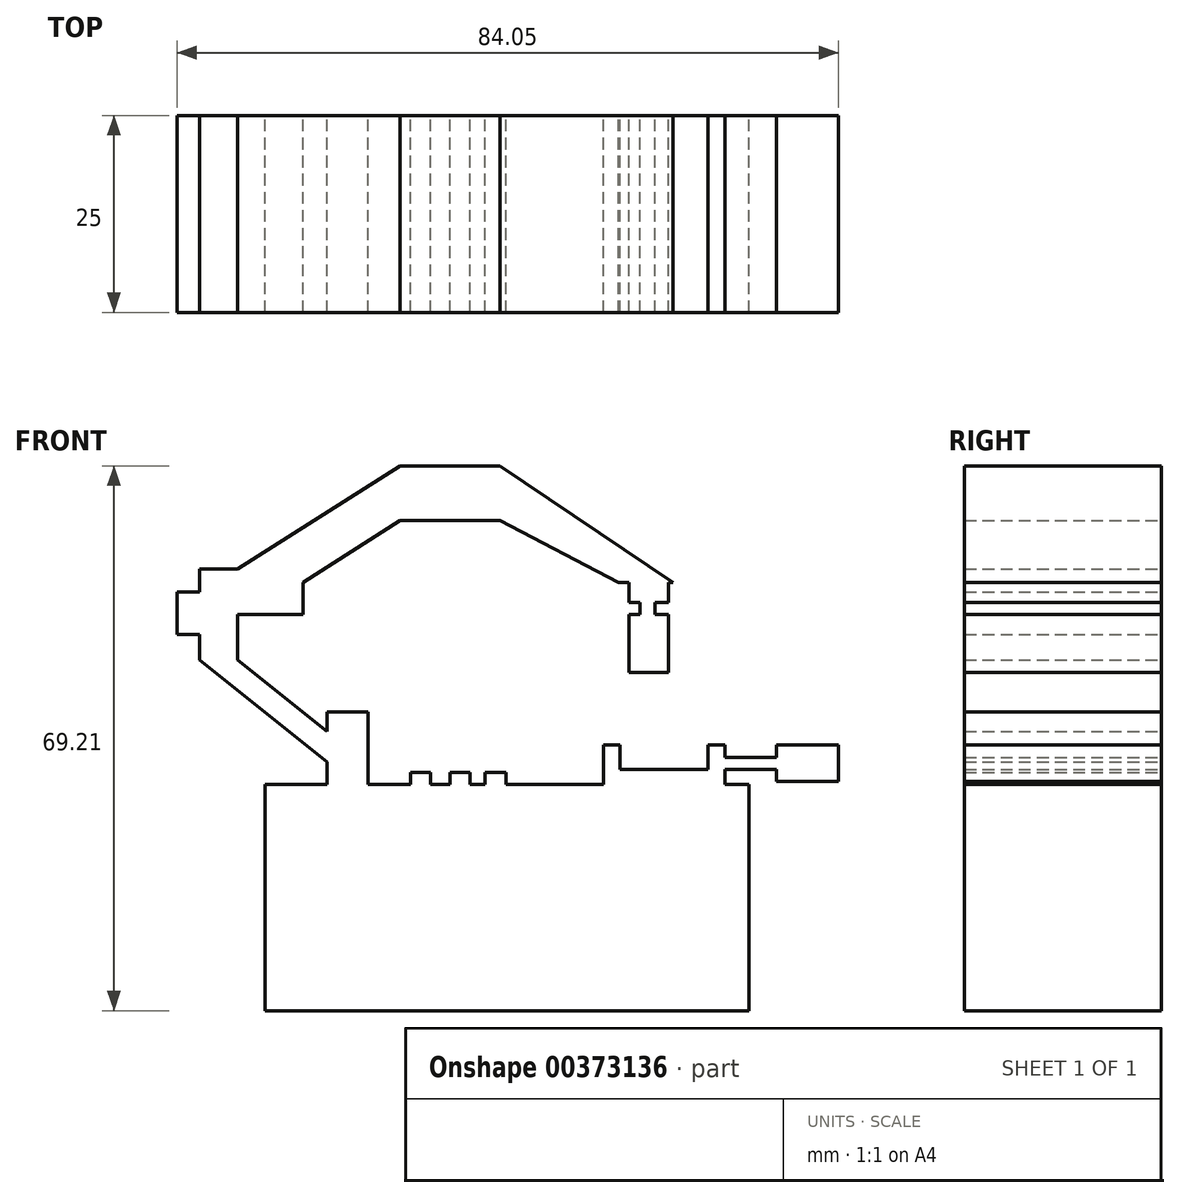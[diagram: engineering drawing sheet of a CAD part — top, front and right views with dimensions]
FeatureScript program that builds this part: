
annotation { "Feature Type Name" : "Feature", "Feature Type Description" : "" }
export const myFeature = defineFeature(function(context is Context, id is Id, definition is map)
    precondition{}
    {
        {
            var Q0;
            Q0=qCreatedBy(makeId("Front.planeOp"),FACE);
            var sketch = newSketch(context, id + "F0", { "sketchPlane" : qUnion([Q0])});
            skLineSegment(sketch, "E0", {"start": v(-61.5, 0) * mm, "end": v(-61.5, -14.36) * mm});
            skLineSegment(sketch, "E1", {"start": v(-61.5, -14.36) * mm, "end": v(0, -14.36) * mm});
            skLineSegment(sketch, "E2", {"start": v(-61.5, 0) * mm, "end": v(-61.5, 14.36) * mm});
            skLineSegment(sketch, "E3", {"start": v(-61.5, 14.36) * mm, "end": v(0, 14.36) * mm});
            skLineSegment(sketch, "E4", {"start": v(0, 14.36) * mm, "end": v(0, -14.36) * mm});
            skLineSegment(sketch, "E5", {"start": v(-61.5, 7.18) * mm, "end": v(-58.03, 9.16) * mm});
            skLineSegment(sketch, "E6", {"start": v(-58.03, 9.16) * mm, "end": v(-54.56, 9.16) * mm});
            skLineSegment(sketch, "E7", {"start": v(-54.56, 9.16) * mm, "end": v(-50.9, 7.18) * mm});
            skLineSegment(sketch, "E8", {"start": v(-50.9, -12.05) * mm, "end": v(-54.56, -14.36) * mm});
            skLineSegment(sketch, "E9", {"start": v(-50.9, -12.05) * mm, "end": v(-50.9, 7.18) * mm});
            skLineSegment(sketch, "E10", {"start": v(-54.56, -14.36) * mm, "end": v(-58.03, -14.36) * mm});
            skLineSegment(sketch, "E11", {"start": v(-58.03, -14.36) * mm, "end": v(-61.5, -12.05) * mm});
            skLineSegment(sketch, "E12", {"start": v(-56.3, 9.16) * mm, "end": v(-50.9, 14.36) * mm});
            skLineSegment(sketch, "E13", {"start": v(-18.5, 14.36) * mm, "end": v(-18.5, 19.37) * mm});
            skLineSegment(sketch, "E14", {"start": v(-18.5, 19.37) * mm, "end": v(-16.39, 19.37) * mm});
            skLineSegment(sketch, "E15", {"start": v(-16.39, 19.37) * mm, "end": v(-16.39, 16.29) * mm});
            skLineSegment(sketch, "E16", {"start": v(-16.39, 16.29) * mm, "end": v(-5.2, 16.29) * mm});
            skLineSegment(sketch, "E17", {"start": v(-5.2, 16.29) * mm, "end": v(-5.2, 19.37) * mm});
            skLineSegment(sketch, "E18", {"start": v(-5.2, 19.37) * mm, "end": v(-3.08, 19.37) * mm});
            skLineSegment(sketch, "E19", {"start": v(-3.08, 19.37) * mm, "end": v(-3.08, 14.36) * mm});
            skLineSegment(sketch, "E20", {"start": v(-3.08, 16.29) * mm, "end": v(3.47, 16.29) * mm});
            skLineSegment(sketch, "E21", {"start": v(3.47, 16.29) * mm, "end": v(3.47, 14.75) * mm});
            skLineSegment(sketch, "E22", {"start": v(3.47, 14.75) * mm, "end": v(11.37, 14.75) * mm});
            skLineSegment(sketch, "E23", {"start": v(11.37, 14.75) * mm, "end": v(11.37, 19.37) * mm});
            skLineSegment(sketch, "E24", {"start": v(11.37, 19.37) * mm, "end": v(3.47, 19.37) * mm});
            skLineSegment(sketch, "E25", {"start": v(3.47, 19.37) * mm, "end": v(3.47, 17.83) * mm});
            skLineSegment(sketch, "E26", {"start": v(3.47, 17.83) * mm, "end": v(-3.08, 17.83) * mm});
            skLineSegment(sketch, "E27", {"start": v(3.47, 17.83) * mm, "end": v(3.47, 16.29) * mm});
            skLineSegment(sketch, "E28", {"start": v(-53.6, 14.36) * mm, "end": v(-53.6, 23.62) * mm});
            skPoint(sketch, "E28.startSnap0", {"position": v(-53.6, 11.76) * mm});
            skLineSegment(sketch, "E29", {"start": v(-48.39, 14.36) * mm, "end": v(-48.39, 23.62) * mm});
            skLineSegment(sketch, "E30", {"start": v(-53.6, 23.62) * mm, "end": v(-48.39, 23.62) * mm});
            skLineSegment(sketch, "E31", {"start": v(-53.6, 21.1) * mm, "end": v(-64.97, 30.17) * mm});
            skLineSegment(sketch, "E32", {"start": v(-64.97, 30.17) * mm, "end": v(-69.79, 30.17) * mm});
            skLineSegment(sketch, "E33", {"start": v(-69.79, 30.17) * mm, "end": v(-53.6, 17.27) * mm});
            skLineSegment(sketch, "E34", {"start": v(-42.99, 14.36) * mm, "end": v(-42.99, 15.9) * mm});
            skLineSegment(sketch, "E35", {"start": v(-42.99, 15.9) * mm, "end": v(-40.48, 15.9) * mm});
            skLineSegment(sketch, "E36", {"start": v(-40.48, 15.9) * mm, "end": v(-40.48, 14.36) * mm});
            skLineSegment(sketch, "E37", {"start": v(-40.48, 14.36) * mm, "end": v(-37.98, 14.36) * mm});
            skLineSegment(sketch, "E38", {"start": v(-37.98, 14.36) * mm, "end": v(-37.98, 15.9) * mm});
            skLineSegment(sketch, "E39", {"start": v(-37.98, 15.9) * mm, "end": v(-35.47, 15.9) * mm});
            skLineSegment(sketch, "E40", {"start": v(-35.47, 15.9) * mm, "end": v(-35.47, 14.36) * mm});
            skLineSegment(sketch, "E41", {"start": v(-35.47, 14.36) * mm, "end": v(-33.54, 14.36) * mm});
            skLineSegment(sketch, "E42", {"start": v(-33.54, 14.36) * mm, "end": v(-33.54, 15.9) * mm});
            skLineSegment(sketch, "E43", {"start": v(-33.54, 15.9) * mm, "end": v(-30.84, 15.9) * mm});
            skLineSegment(sketch, "E44", {"start": v(-30.84, 15.9) * mm, "end": v(-30.84, 14.36) * mm});
            skLineSegment(sketch, "E45", {"start": v(-69.79, 30.17) * mm, "end": v(-69.79, 41.74) * mm});
            skLineSegment(sketch, "E46", {"start": v(-64.97, 30.17) * mm, "end": v(-64.97, 41.74) * mm});
            skLineSegment(sketch, "E47", {"start": v(-69.79, 41.74) * mm, "end": v(-64.97, 41.74) * mm});
            skLineSegment(sketch, "E48", {"start": v(-69.79, 33.45) * mm, "end": v(-72.68, 33.45) * mm});
            skLineSegment(sketch, "E49", {"start": v(-72.68, 33.45) * mm, "end": v(-72.68, 38.84) * mm});
            skLineSegment(sketch, "E50", {"start": v(-72.68, 38.84) * mm, "end": v(-69.79, 38.84) * mm});
            skLineSegment(sketch, "E51", {"start": v(-64.97, 41.74) * mm, "end": v(-56.68, 41.74) * mm});
            skLineSegment(sketch, "E52", {"start": v(-56.68, 41.74) * mm, "end": v(-56.68, 35.95) * mm});
            skLineSegment(sketch, "E53", {"start": v(-56.68, 35.95) * mm, "end": v(-64.97, 35.95) * mm});
            skLineSegment(sketch, "E54", {"start": v(-64.97, 41.74) * mm, "end": v(-44.34, 54.85) * mm});
            skLineSegment(sketch, "E55", {"start": v(-44.34, 54.85) * mm, "end": v(-31.62, 54.85) * mm});
            skLineSegment(sketch, "E56", {"start": v(-31.62, 54.85) * mm, "end": v(-31.62, 47.9) * mm});
            skLineSegment(sketch, "E57", {"start": v(-31.62, 47.9) * mm, "end": v(-44.34, 47.9) * mm});
            skLineSegment(sketch, "E58", {"start": v(-44.34, 47.9) * mm, "end": v(-44.34, 54.85) * mm});
            skLineSegment(sketch, "E59", {"start": v(-44.34, 47.9) * mm, "end": v(-56.68, 40.06) * mm});
            skLineSegment(sketch, "E60", {"start": v(-31.62, 47.9) * mm, "end": v(-16.58, 40.06) * mm});
            skLineSegment(sketch, "E61", {"start": v(-31.62, 54.85) * mm, "end": v(-9.64, 40.06) * mm});
            skLineSegment(sketch, "E62", {"start": v(-16.58, 40.06) * mm, "end": v(-9.64, 40.06) * mm});
            skLineSegment(sketch, "E63", {"start": v(-15.23, 40.06) * mm, "end": v(-15.23, 37.5) * mm});
            skLineSegment(sketch, "E64", {"start": v(-15.23, 37.5) * mm, "end": v(-13.88, 37.5) * mm});
            skLineSegment(sketch, "E65", {"start": v(-13.88, 37.5) * mm, "end": v(-13.88, 35.95) * mm});
            skLineSegment(sketch, "E66", {"start": v(-13.88, 35.95) * mm, "end": v(-15.23, 35.95) * mm});
            skLineSegment(sketch, "E67", {"start": v(-15.23, 35.95) * mm, "end": v(-15.23, 28.63) * mm});
            skLineSegment(sketch, "E68", {"start": v(-15.23, 28.63) * mm, "end": v(-10.22, 28.63) * mm});
            skLineSegment(sketch, "E69", {"start": v(-10.22, 28.63) * mm, "end": v(-10.22, 35.95) * mm});
            skLineSegment(sketch, "E70", {"start": v(-10.22, 35.95) * mm, "end": v(-11.95, 35.95) * mm});
            skLineSegment(sketch, "E71", {"start": v(-11.95, 35.95) * mm, "end": v(-11.95, 37.5) * mm});
            skLineSegment(sketch, "E72", {"start": v(-11.95, 37.5) * mm, "end": v(-10.22, 37.5) * mm});
            skLineSegment(sketch, "E73", {"start": v(-10.22, 37.5) * mm, "end": v(-10.22, 40.06) * mm});
            skLineSegment(sketch, "E74", {"start": v(-12.72, 28.63) * mm, "end": v(-12.72, 23.23) * mm});
            skLineSegment(sketch, "E75", {"start": v(-72.68, 33.45) * mm, "end": v(-69.79, 31.14) * mm});
            skLineSegment(sketch, "E76", {"start": v(-61.5, 5.1) * mm, "end": v(-50.9, 5.1) * mm});
            skLineSegment(sketch, "E77", {"start": v(-61.5, 1.83) * mm, "end": v(-50.9, 1.83) * mm});
            skSolve(sketch);
        }
        {
            var Q0;
            {var subQ0=sQuery(id+"F0.wireOp",EDGE,"E8");Q0=makeQuery(id+"F0.imprint","IMPRINT",FACE,{"disambiguationData":[TD([[makeQuery(id+"F0.imprint","IMPRINT",EDGE,{"derivedFrom":subQ0}),-1.0]])]});}
            var Q1;
            {var subQ0=sQuery(id+"F0.wireOp",EDGE,"E76");Q1=makeQuery(id+"F0.imprint","IMPRINT",FACE,{"disambiguationData":[TD([[makeQuery(id+"F0.imprint","IMPRINT",EDGE,{"derivedFrom":subQ0}),-1.0]])]});}
            var Q2;
            {var subQ1=sQuery(id+"F0.wireOp",EDGE,"E5");Q2=makeQuery(id+"F0.imprint","IMPRINT",FACE,{"disambiguationData":[TD([[makeQuery(id+"F0.imprint","IMPRINT",EDGE,{"derivedFrom":subQ1}),-1.0]])]});}
            var Q3;
            {var subQ0=sQuery(id+"F0.wireOp",EDGE,"E4");Q3=makeQuery(id+"F0.imprint","IMPRINT",FACE,{"disambiguationData":[TD([[makeQuery(id+"F0.imprint","IMPRINT",EDGE,{"derivedFrom":subQ0}),-1.0]])]});}
            var Q4;
            {var subQ3=sQuery(id+"F0.wireOp",EDGE,"E11");Q4=makeQuery(id+"F0.imprint","IMPRINT",FACE,{"disambiguationData":[TD([[makeQuery(id+"F0.imprint","IMPRINT",EDGE,{"derivedFrom":subQ3}),1.0]])]});}
            var Q5;
            {var subQ0=sQuery(id+"F0.wireOp",EDGE,"E5");Q5=makeQuery(id+"F0.imprint","IMPRINT",FACE,{"disambiguationData":[TD([[makeQuery(id+"F0.imprint","IMPRINT",EDGE,{"derivedFrom":subQ0}),1.0]])]});}
            var Q6;
            {var subQ0=sQuery(id+"F0.wireOp",EDGE,"E34");Q6=makeQuery(id+"F0.imprint","IMPRINT",FACE,{"disambiguationData":[TD([[makeQuery(id+"F0.imprint","IMPRINT",EDGE,{"derivedFrom":subQ0}),-1.0]])]});}
            var Q7;
            {var subQ0=sQuery(id+"F0.wireOp",EDGE,"E48");Q7=makeQuery(id+"F0.imprint","IMPRINT",FACE,{"disambiguationData":[TD([[makeQuery(id+"F0.imprint","IMPRINT",EDGE,{"derivedFrom":subQ0}),-1.0]])]});}
            var Q8;
            {var subQ3=sQuery(id+"F0.wireOp",EDGE,"E32");Q8=makeQuery(id+"F0.imprint","IMPRINT",FACE,{"disambiguationData":[TD([[makeQuery(id+"F0.imprint","IMPRINT",EDGE,{"derivedFrom":subQ3}),-1.0]])]});}
            var Q9;
            {var subQ0=sQuery(id+"F0.wireOp",EDGE,"E31");Q9=makeQuery(id+"F0.imprint","IMPRINT",FACE,{"disambiguationData":[TD([[makeQuery(id+"F0.imprint","IMPRINT",EDGE,{"derivedFrom":subQ0}),1.0]])]});}
            var Q10;
            {var subQ6=sQuery(id+"F0.wireOp",EDGE,"E29");Q10=makeQuery(id+"F0.imprint","IMPRINT",FACE,{"disambiguationData":[TD([[makeQuery(id+"F0.imprint","IMPRINT",EDGE,{"derivedFrom":subQ6}),1.0]])]});}
            var Q11;
            {var subQ0=sQuery(id+"F0.wireOp",EDGE,"E38");Q11=makeQuery(id+"F0.imprint","IMPRINT",FACE,{"disambiguationData":[TD([[makeQuery(id+"F0.imprint","IMPRINT",EDGE,{"derivedFrom":subQ0}),-1.0]])]});}
            var Q12;
            {var subQ0=sQuery(id+"F0.wireOp",EDGE,"E42");Q12=makeQuery(id+"F0.imprint","IMPRINT",FACE,{"disambiguationData":[TD([[makeQuery(id+"F0.imprint","IMPRINT",EDGE,{"derivedFrom":subQ0}),-1.0]])]});}
            var Q13;
            {var subQ0=sQuery(id+"F0.wireOp",EDGE,"E13");Q13=makeQuery(id+"F0.imprint","IMPRINT",FACE,{"disambiguationData":[TD([[makeQuery(id+"F0.imprint","IMPRINT",EDGE,{"derivedFrom":subQ0}),-1.0]])]});}
            var Q14;
            {var subQ0=sQuery(id+"F0.wireOp",EDGE,"E20");Q14=makeQuery(id+"F0.imprint","IMPRINT",FACE,{"disambiguationData":[TD([[makeQuery(id+"F0.imprint","IMPRINT",EDGE,{"derivedFrom":subQ0}),1.0]])]});}
            var Q15;
            Q15=makeQuery(id+"F0.imprint","IMPRINT",FACE,{"disambiguationData":[TD([[makeQuery(id+"F0.imprint","IMPRINT",EDGE,{"derivedFrom":sQuery(id+"F0.wireOp",EDGE,"E21")}),1.0]])]});
            var Q16;
            {var subQ4=sQuery(id+"F0.wireOp",EDGE,"E63");Q16=makeQuery(id+"F0.imprint","IMPRINT",FACE,{"disambiguationData":[TD([[makeQuery(id+"F0.imprint","IMPRINT",EDGE,{"derivedFrom":subQ4}),1.0]])]});}
            var Q17;
            Q17=makeQuery(id+"F0.imprint","IMPRINT",FACE,{"disambiguationData":[TD([[makeQuery(id+"F0.imprint","IMPRINT",EDGE,{"derivedFrom":sQuery(id+"F0.wireOp",EDGE,"E56")}),1.0]])]});
            var Q18;
            Q18=makeQuery(id+"F0.imprint","IMPRINT",FACE,{"disambiguationData":[TD([[makeQuery(id+"F0.imprint","IMPRINT",EDGE,{"derivedFrom":sQuery(id+"F0.wireOp",EDGE,"E55")}),-1.0]])]});
            var Q19;
            {var subQ1=sQuery(id+"F0.wireOp",EDGE,"E51");Q19=makeQuery(id+"F0.imprint","IMPRINT",FACE,{"disambiguationData":[TD([[makeQuery(id+"F0.imprint","IMPRINT",EDGE,{"derivedFrom":subQ1}),1.0]])]});}
            var Q20;
            {var subQ3=sQuery(id+"F0.wireOp",EDGE,"E51");Q20=makeQuery(id+"F0.imprint","IMPRINT",FACE,{"disambiguationData":[TD([[makeQuery(id+"F0.imprint","IMPRINT",EDGE,{"derivedFrom":subQ3}),-1.0]])]});}
            extrude(context, id + "F1", {"entities" : qUnion([Q0, Q1, Q2, Q3, Q4, Q5, Q6, Q7, Q8, Q9, Q10, Q11, Q12, Q13, Q14, Q15, Q16, Q17, Q18, Q19, Q20]), "depth" : 25 * mm});
        }
    });
